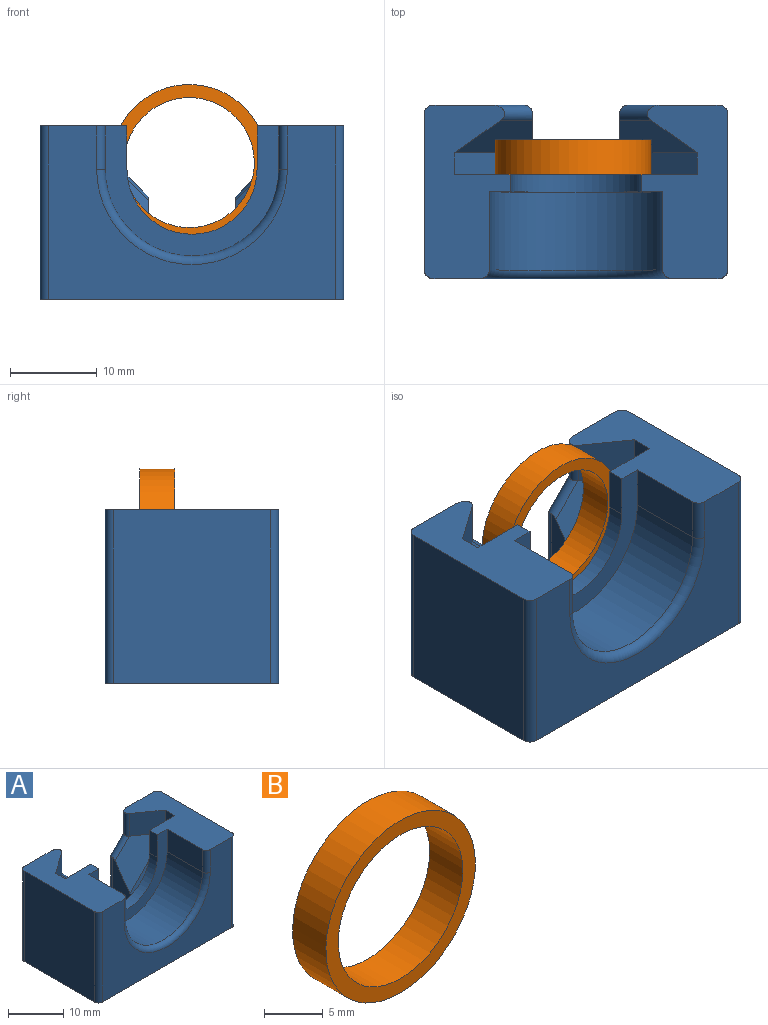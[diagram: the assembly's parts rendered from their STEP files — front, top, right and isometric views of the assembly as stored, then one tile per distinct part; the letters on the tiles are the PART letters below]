
ASSEMBLY  parts=2 mates=1
PART A: 41 faces, bbox 35x20x20 mm
  f0: plane 28x20mm, normal (0,1,0), area 196.6mm2, adj f3,f4,f11,f15,f16,f17,f29,f30
  f1: plane 20x10.5mm, normal (0,1,0), area 185.2mm2, adj f3,f18,f19,f25,f35,f40
  f2: plane 20x10.5mm, normal (0,1,0), area 185.2mm2, adj f3,f20,f21,f24,f27,f33
  f3: plane 35x20mm, normal (0,0,-1), area 619.1mm2, adj f0,f1,f2,f6,f7,f8,f13,f14
  f4: plane 10x10mm, normal (0.71,0,0.71), area 32.1mm2, adj f0,f12,f14,f17,f39
  f5: plane 9x9mm, normal (-0.5,-0.71,0.5), area 47.9mm2, adj f11,f13,f20,f28
  f6: plane 33x20mm, normal (0,-1,0), area 359.9mm2, adj f3,f22,f23,f26,f32,f33,f36,f40
  f7: plane 20x18mm, normal (1,0,0), area 360mm2, adj f3,f23,f24,f33
  f8: plane 20x18mm, normal (-1,0,0), area 360mm2, adj f3,f25,f26,f40
  f9: cylinder r=10mm len=20mm, axis (0,-1,0), area 282.7mm2, adj f10,f22,f31,f37
  f10: plane 20x15mm, normal (0,-1,0), area 93.7mm2, adj f9,f15,f30,f31,f33,f37,f38,f40
  f11: plane 10x10mm, normal (-0.71,0,0.71), area 32.1mm2, adj f0,f5,f13,f16,f29
  f12: plane 9x9mm, normal (0.5,-0.71,0.5), area 47.9mm2, adj f4,f14,f18,f34
  f13: plane 11.78x6mm, normal (-1,0,0), area 50.2mm2, adj f3,f5,f11,f16,f20,f21
  f14: plane 11.78x6mm, normal (1,0,0), area 50.2mm2, adj f3,f4,f12,f17,f18,f19
  f15: cylinder r=7.5mm len=15mm, axis (0,-1,0), area 47.1mm2, adj f0,f10,f30,f38
  f16: cylinder r=1mm len=6mm, axis (0,0,1), area 8.9mm2, adj f0,f3,f11,f13
  f17: cylinder r=1mm len=6mm, axis (0,0,-1), area 8.9mm2, adj f0,f3,f4,f14
  f18: cylinder r=1mm len=4.84mm, axis (0.71,0,-0.71), area 11.2mm2, adj f1,f12,f14,f19,f35
  f19: cylinder r=1mm len=11.78mm, axis (0,0,1), area 18.3mm2, adj f1,f3,f14,f18
  f20: cylinder r=1mm len=4.84mm, axis (-0.71,0,-0.71), area 11.2mm2, adj f2,f5,f13,f21,f27
  f21: cylinder r=1mm len=11.78mm, axis (0,0,-1), area 18.3mm2, adj f2,f3,f13,f20
  f22: torus R=11mm, axis (0,-1,0), area 51.1mm2, adj f6,f9,f32,f36
  f23: cylinder r=1mm len=20mm, axis (0,0,1), area 31.4mm2, adj f3,f6,f7,f33
  f24: cylinder r=1mm len=20mm, axis (0,0,-1), area 31.4mm2, adj f2,f3,f7,f33
  f25: cylinder r=1mm len=20mm, axis (0,0,1), area 31.4mm2, adj f1,f3,f8,f40
  f26: cylinder r=1mm len=20mm, axis (0,0,-1), area 31.4mm2, adj f3,f6,f8,f40
  f27: extruded ~5x1.71mm, area 13.8mm2, adj f2,f20,f28,f33
  f28: plane 5.36x5mm, normal (-0.58,-0.82,0), area 32.8mm2, adj f5,f27,f29,f33
  f29: plane 5x2.5mm, normal (-1,0,0), area 12.5mm2, adj f0,f11,f28,f33
  f30: plane 5x2mm, normal (-1,0,0), area 10mm2, adj f0,f10,f15,f33
  f31: plane 9x5mm, normal (-1,0,0), area 45mm2, adj f9,f10,f32,f33
  f32: cylinder r=1mm len=5mm, axis (0,0,-1), area 7.9mm2, adj f6,f22,f31,f33
  f33: plane 20x10mm, normal (0,0,1), area 142mm2, adj f0,f2,f6,f7,f10,f23,f24,f27
  f34: plane 5.36x5mm, normal (0.58,-0.82,0), area 32.8mm2, adj f12,f35,f39,f40
  f35: extruded ~5x1.71mm, area 13.8mm2, adj f1,f18,f34,f40
  f36: cylinder r=1mm len=5mm, axis (0,0,-1), area 7.9mm2, adj f6,f22,f37,f40
  f37: plane 9x5mm, normal (1,0,0), area 45mm2, adj f9,f10,f36,f40
  f38: plane 5x2mm, normal (1,0,0), area 10mm2, adj f0,f10,f15,f40
  f39: plane 5x2.5mm, normal (1,0,0), area 12.5mm2, adj f0,f4,f34,f40
  f40: plane 20x10mm, normal (0,0,1), area 142mm2, adj f0,f1,f6,f8,f10,f25,f26,f34
PART B: 4 faces, bbox 18x4x18 mm
  f0: cylinder r=7.5mm len=15mm, axis (0,1,0), area 188.5mm2, adj f2,f3
  f1: cylinder r=9mm len=18mm, axis (0,1,0), area 226.2mm2, adj f2,f3
  f2: plane 18x18mm, normal (0,-1,0), area 77.8mm2, adj f0,f1
  f3: plane 18x18mm, normal (0,1,0), area 77.8mm2, adj f0,f1
PLACE A t=(-1.98,0.36,-2.56)mm
PLACE B t=(-2.29,6.36,13.21)mm
MATE planar B.f1 <-> A.f0  axis (0,-1,0) through (-2.29,2.36,13.21)mm
